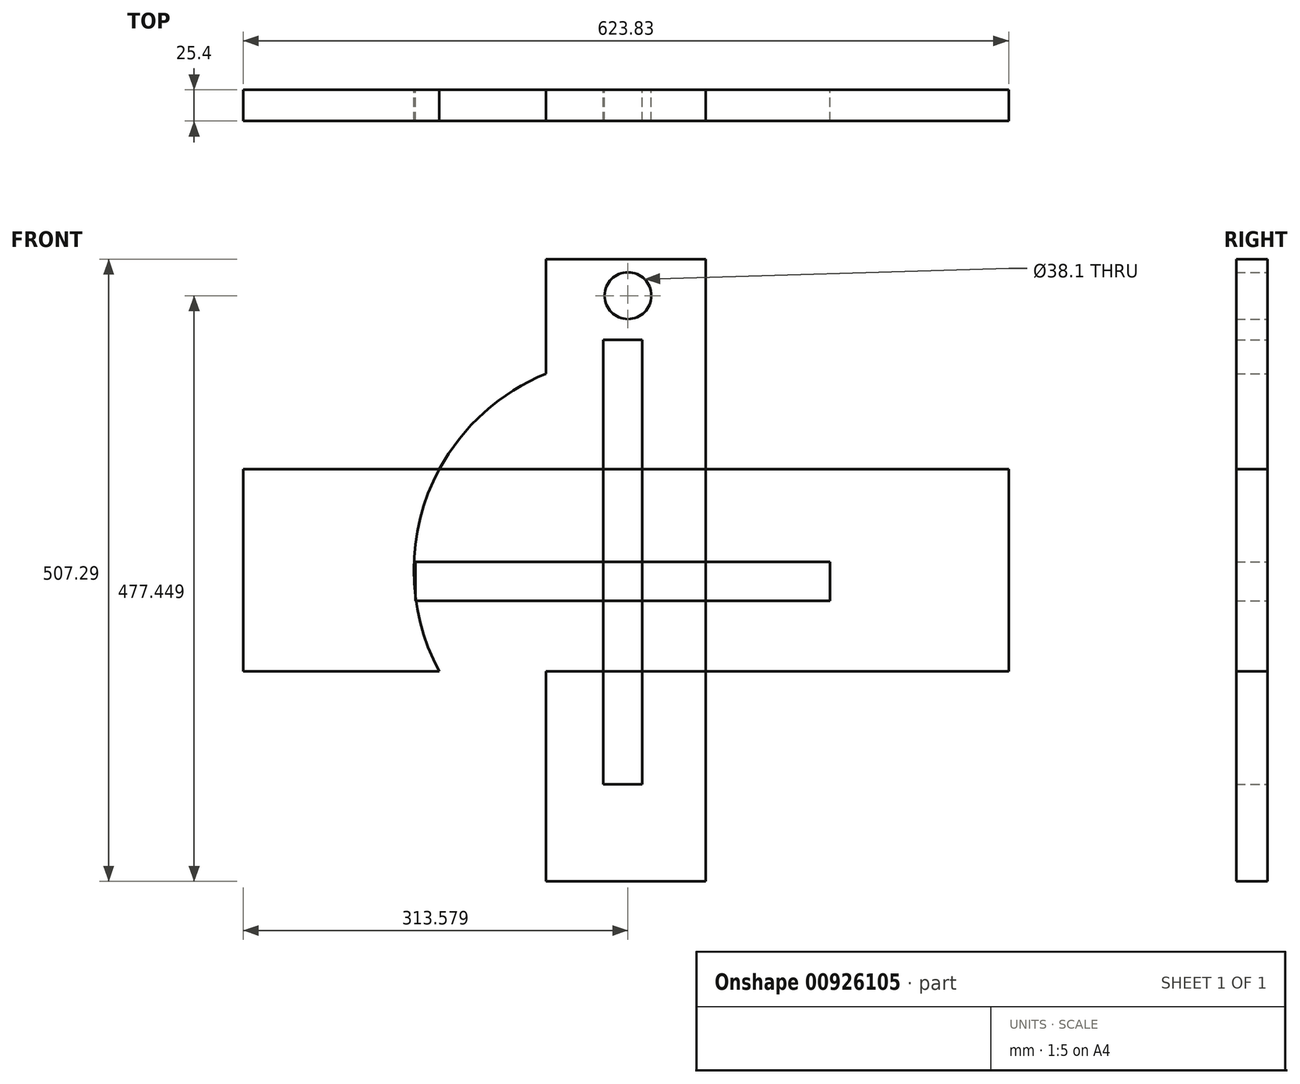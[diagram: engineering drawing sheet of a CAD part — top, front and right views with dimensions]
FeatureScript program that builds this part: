
annotation { "Feature Type Name" : "Feature", "Feature Type Description" : "" }
export const myFeature = defineFeature(function(context is Context, id is Id, definition is map)
    precondition{}
    {
        {
            var Q0;
            Q0=qCreatedBy(makeId("Front.planeOp"),FACE);
            var sketch = newSketch(context, id + "F0", { "sketchPlane" : qUnion([Q0])});
            skCircle(sketch, "E0", {"center": v(752.9, 542.45) * mm, "radius": 172.92 * mm});
            skLineSegment(sketch, "E1.bottom", {"start": v(441, 624.71) * mm, "end": v(1064.82, 624.71) * mm});
            skLineSegment(sketch, "E1.top", {"start": v(441, 460.19) * mm, "end": v(1064.82, 460.19) * mm});
            skLineSegment(sketch, "E1.left", {"start": v(441, 624.71) * mm, "end": v(441, 460.19) * mm});
            skLineSegment(sketch, "E1.right", {"start": v(1064.82, 624.71) * mm, "end": v(1064.82, 460.19) * mm});
            skLineSegment(sketch, "E2.bottom", {"start": v(818.03, 796.1) * mm, "end": v(687.78, 796.1) * mm});
            skLineSegment(sketch, "E2.top", {"start": v(818.03, 288.8) * mm, "end": v(687.78, 288.8) * mm});
            skLineSegment(sketch, "E2.left", {"start": v(818.03, 796.1) * mm, "end": v(818.03, 288.8) * mm});
            skLineSegment(sketch, "E2.right", {"start": v(687.78, 796.1) * mm, "end": v(687.78, 288.8) * mm});
            skSolve(sketch);
        }
        {
            var Q0;
            {var subQ5=sQuery(id+"F0.wireOp",EDGE,"E2.top");Q0=makeQuery(id+"F0.imprint","IMPRINT",FACE,{"disambiguationData":[TD([[makeQuery(id+"F0.imprint","IMPRINT",EDGE,{"derivedFrom":subQ5}),-1.0]])]});}
            var Q1;
            {var subQ5=sQuery(id+"F0.wireOp",EDGE,"E1.left");Q1=makeQuery(id+"F0.imprint","IMPRINT",FACE,{"disambiguationData":[TD([[makeQuery(id+"F0.imprint","IMPRINT",EDGE,{"derivedFrom":subQ5}),1.0]])]});}
            var Q2;
            {var subQ0=sQuery(id+"F0.wireOp",EDGE,"E1.top");var subQ1=sQuery(id+"F0.wireOp",EDGE,"E0");var subQ2=makeQuery(id+"F0.imprint","INTERSECT",VERTEX,{"disambiguationData":[OD(0.0)],"derivedFrom":[subQ1,subQ0]});Q2=makeQuery(id+"F0.imprint","IMPRINT",FACE,{"disambiguationData":[TD([[makeQuery(id+"F0.imprint","IMPRINT",EDGE,{"disambiguationData":[TD([[subQ2,-1.0]])],"derivedFrom":subQ1}),1.0]])]});}
            var Q3;
            {var subQ5=sQuery(id+"F0.wireOp",EDGE,"E1.right");Q3=makeQuery(id+"F0.imprint","IMPRINT",FACE,{"disambiguationData":[TD([[makeQuery(id+"F0.imprint","IMPRINT",EDGE,{"derivedFrom":subQ5}),-1.0]])]});}
            var Q4;
            {var subQ0=sQuery(id+"F0.wireOp",EDGE,"E2.left");var subQ1=sQuery(id+"F0.wireOp",EDGE,"E0");var subQ2=makeQuery(id+"F0.imprint","INTERSECT",VERTEX,{"disambiguationData":[OD(1.0)],"derivedFrom":[subQ1,subQ0]});Q4=makeQuery(id+"F0.imprint","IMPRINT",FACE,{"disambiguationData":[TD([[makeQuery(id+"F0.imprint","IMPRINT",EDGE,{"disambiguationData":[TD([[subQ2,-1.0]])],"derivedFrom":subQ1}),1.0]])]});}
            var Q5;
            {var subQ0=sQuery(id+"F0.wireOp",EDGE,"E2.right");var subQ1=sQuery(id+"F0.wireOp",EDGE,"E0");var subQ2=makeQuery(id+"F0.imprint","INTERSECT",VERTEX,{"disambiguationData":[OD(0.0)],"derivedFrom":[subQ1,subQ0]});Q5=makeQuery(id+"F0.imprint","IMPRINT",FACE,{"disambiguationData":[TD([[makeQuery(id+"F0.imprint","IMPRINT",EDGE,{"disambiguationData":[TD([[subQ2,-1.0]])],"derivedFrom":subQ1}),1.0]])]});}
            var Q6;
            {var subQ5=sQuery(id+"F0.wireOp",EDGE,"E2.bottom");Q6=makeQuery(id+"F0.imprint","IMPRINT",FACE,{"disambiguationData":[TD([[makeQuery(id+"F0.imprint","IMPRINT",EDGE,{"derivedFrom":subQ5}),1.0]])]});}
            var Q7;
            {var subQ0=sQuery(id+"F0.wireOp",EDGE,"E2.left");var subQ1=sQuery(id+"F0.wireOp",EDGE,"E0");var subQ2=makeQuery(id+"F0.imprint","INTERSECT",VERTEX,{"disambiguationData":[OD(0.0)],"derivedFrom":[subQ1,subQ0]});Q7=makeQuery(id+"F0.imprint","IMPRINT",FACE,{"disambiguationData":[TD([[makeQuery(id+"F0.imprint","IMPRINT",EDGE,{"disambiguationData":[TD([[subQ2,1.0]])],"derivedFrom":subQ1}),1.0]])]});}
            extrude(context, id + "F1", {"entities" : qUnion([Q0, Q1, Q2, Q3, Q4, Q5, Q6, Q7]), "depth" : 25.4 * mm, "offsetDistance" : 25.4 * mm});
        }
        {
            var Q0;
            Q0=qCreatedBy(makeId("Front.planeOp"),FACE);
            var sketch = newSketch(context, id + "F2", { "sketchPlane" : qUnion([Q0])});
            skLineSegment(sketch, "E3.bottom", {"start": v(919.28, 549.12) * mm, "end": v(581.35, 549.12) * mm});
            skLineSegment(sketch, "E3.top", {"start": v(919.28, 517.6) * mm, "end": v(581.35, 517.6) * mm});
            skLineSegment(sketch, "E3.left", {"start": v(919.28, 549.12) * mm, "end": v(919.28, 517.6) * mm});
            skLineSegment(sketch, "E3.right", {"start": v(581.35, 549.12) * mm, "end": v(581.35, 517.6) * mm});
            skPoint(sketch, "E3.middle", {"position": v(750.32, 533.36) * mm});
            skLineSegment(sketch, "E4.bottom", {"start": v(766.13, 368.02) * mm, "end": v(734.5, 368.02) * mm});
            skLineSegment(sketch, "E4.top", {"start": v(766.13, 730.23) * mm, "end": v(734.5, 730.23) * mm});
            skLineSegment(sketch, "E4.left", {"start": v(766.13, 368.02) * mm, "end": v(766.13, 730.23) * mm});
            skLineSegment(sketch, "E4.right", {"start": v(734.5, 368.02) * mm, "end": v(734.5, 730.23) * mm});
            skPoint(sketch, "E4.middle", {"position": v(750.32, 549.12) * mm});
            skSolve(sketch);
        }
        {
            var Q0;
            {var subQ5=sQuery(id+"F2.wireOp",EDGE,"E4.bottom");Q0=makeQuery(id+"F2.imprint","IMPRINT",FACE,{"disambiguationData":[TD([[makeQuery(id+"F2.imprint","IMPRINT",EDGE,{"derivedFrom":subQ5}),-1.0]])]});}
            var Q1;
            {var subQ5=sQuery(id+"F2.wireOp",EDGE,"E4.top");Q1=makeQuery(id+"F2.imprint","IMPRINT",FACE,{"disambiguationData":[TD([[makeQuery(id+"F2.imprint","IMPRINT",EDGE,{"derivedFrom":subQ5}),1.0]])]});}
            var Q2;
            {var subQ0=sQuery(id+"F2.wireOp",EDGE,"E3.left");Q2=makeQuery(id+"F2.imprint","IMPRINT",FACE,{"disambiguationData":[TD([[makeQuery(id+"F2.imprint","IMPRINT",EDGE,{"derivedFrom":subQ0}),-1.0]])]});}
            var Q3;
            {var subQ0=sQuery(id+"F2.wireOp",EDGE,"E3.right");Q3=makeQuery(id+"F2.imprint","IMPRINT",FACE,{"disambiguationData":[TD([[makeQuery(id+"F2.imprint","IMPRINT",EDGE,{"derivedFrom":subQ0}),1.0]])]});}
            extrude(context, id + "F3", {"entities" : qUnion([Q0, Q1, Q2, Q3]), "depth" : 25.4 * mm, "offsetDistance" : 25.4 * mm});
        }
        {
            var Q0;
            Q0=qCreatedBy(makeId("Front.planeOp"),FACE);
            var sketch = newSketch(context, id + "F4", { "sketchPlane" : qUnion([Q0])});
            skCircle(sketch, "E5", {"center": v(754.57, 766.25) * mm, "radius": 28.2 * mm});
            skSolve(sketch);
        }
        {
            var Q0;
            Q0=sQuery(id+"F4.wireOp",VERTEX,"E5.center");
            var Q1;
            Q1=makeQuery(id+"F1.opExtrude","SWEPT_BODY",BODY,{"disambiguationData":[OSD([sQuery(id+"F0.wireOp",EDGE,"E0"),sQuery(id+"F0.wireOp",EDGE,"E2.bottom"),sQuery(id+"F0.wireOp",EDGE,"E2.left"),sQuery(id+"F0.wireOp",EDGE,"E2.right")])]});
            hole(context, id + "F5", {"style" : HoleStyle.SIMPLE, "endStyle" : HoleEndStyle.THROUGH, "oppositeDirection" : true, "holeDiameter" : 38.1 * mm, "majorDiameter" : 6.35 * mm, "isTappedThrough" : true, "tappedDepth" : 12.7 * mm, "tapClearance" : 3, "locations" : qUnion([Q0]), "scope" : qUnion([Q1])});
        }
    });
